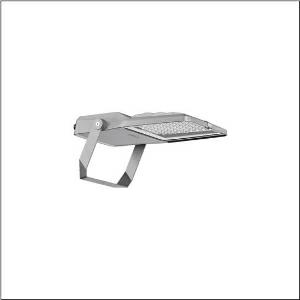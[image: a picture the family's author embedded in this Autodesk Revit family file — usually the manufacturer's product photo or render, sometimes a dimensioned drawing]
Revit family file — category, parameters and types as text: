
# Revit family: floodlight_fl_21_iq_mini___pl61_5xa7772c1c1a_a98f
name_source: partatom
category: Lighting Fixtures
units: mm (PartAtom-declared; Revit-internal decimal feet)

## family parameters
Cut with Voids When Loaded = No
Host = Face
Light Source = No
Part Type = Normal
Room Calculation Point = No
Round Connector Dimension = Use Diameter
Shared = No

## types (1)
- --- (1 x LED, 9930 lm, 87.2 W, 2200K)
    Apparent Load = 87 VA
    CIE Flux Codes = 33 65 98 100 100
    Color Rendering = 70
    Color Temperature = 2200K
    Default Elevation = 1800 mm
    Description = Floodlight FL 21 iQ mini, floodlight, primary light control with lens, of PMMA, primary optical cover: protective disc, of toughened safety glass, transparent, light distribution: PL61, light emission: direct distribution, installation type: surface-mounted, lamps: LED, High Power LED, rated values: 9.930lm | 87,2W | 113,9lm/W (begin service life); end service life: 9.930lm | 92,1W; at 50% lumin. flux: 4.965lm | 40,1W | 123,8lm/W, colour temperature: 2200K, colour rendering: CRI > 70, light colour: 722, light setting 1 begin service life: 100% | 9.930lm | 87,2W | 113,9lm/W | 2.200K, light setting 1 end service life: 92,1W, further light settings possible, control: Street-Remote, Auto-Match, Temp-Guard, Night-Set, Smart-Wire, Desk-Remote (wireless, voltage-free reading and setting of iQ features in the workshop via application-optimized NFC function/RFID function), optimised constant luminous flux control (CLO 2.0), pre-setting: linear dimming characteristic, with terminal, 6-pole, mains connection: 220..240V, AC, 50/60Hz, luminaire housing, of diecast aluminium, powder-coated, SITECO metallic grey (DB 702S), corrosivity category C5 mid according to DIN EN ISO 12944suitable for swimming poolschlorine-resistant, sealing non-destructively replaceable, mounting bracket, of steel, galvanised, powder-coated, SITECO metallic grey (DB 702S), protection rating (complete): IP66, insulation class (complete): insulation class II (safety insulation), certification: CE, ENEC, VDE, protection symbol: D, impact resistance: IK08, permissible operating ambient temperature: -40..+40°C, permissible operating ambient temperature for outdoor applications: -40..+50°C, standard: DIN EN 12944, LABS conformity tested according to VDMA 24364:2018-05, packaging unit: 1 piece

Light Distribution: PL61
    Height = 70 mm
    Lamp = 1 x LED
    Lamp Light Flux = 9930 lm
    Lamp Power = 87.2 W
    Lamp count = 1
    Length = 485 mm
    Luminous efficacy = 114 lm/W
    Manufacturer = Siteco
    ModVariant = No
    Model = 5XA7772C1C1A
    Number of Poles = 1
    OnlyDefault = Yes
    Power Factor = 1
    Product Name = Floodlight FL 21 iQ mini | PL61
    Product group = floodlight | pylon annexe
    ProductGroupID = 6201
    Protection Class = Protection class II
    Protection Degree = IP 66
    RLX_Detail_Level = 1
    RLX_Emergency_Light_Flux = 0 lm
    RLX_Emergency_Type = 0
    RLX_Emergency_Type_DB = No
    RlxData = <blob elided: 96561 chars, md5=af191a61>
    Socket = socket
    Standby Power = 0 W
    System Light Flux = 9930 lm
    System Power = 87 W
    Type Comments = factory setting: luminous flux: 100 % | dim-lin: 254 | 456 mA
    Type Image = l_1006845.jpg
    URL = http://relux.com
    VarID = @adj_172637
    Voltage = 0 V
    Weight = 0.00 kg
    Width = 337 mm

## geometry (parser evidence)
native form markers: Blend x4, Sweep x12
no freeform markers — native parametric forms only
